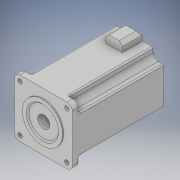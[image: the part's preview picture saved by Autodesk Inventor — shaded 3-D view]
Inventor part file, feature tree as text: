
AUTODESK INVENTOR PART (.ipt)
format: ipt  version: 2018 (Build 220112000, 112)  size: 386,048 bytes
history: native  units: mm
features: extrude x13, sketch x13, chamfer x5, projected_geometry x4, fillet x3, hole x1, plane x1
ambient origin geometry x8: Origin, YZ Plane, XZ Plane, XY Plane, X Axis, Y Axis, Z Axis, Center Point
bodies: Solid1 (feature_tree)
feature tree (40):
  extrude  "Extrusion1"  Depth=86.0mm
  extrude  "Extrusion2"  Depth=140.0mm
  extrude  "Extrusion3"  Depth=1.5mm
  hole  "Hole1"  [1 undecoded]
  plane  "Work Plane1"
  extrude  "Extrusion4"  Depth=13.0mm TaperAngle=0.0deg
  sketch  "Sketch6"  dims[d13=3.0mm d14=6.0mm d15=4.0mm d16=2.0mm d17=90.0deg d18=13.0mm d19=0.0mm d24=2.438mm d25=0.0mm]
  extrude  "Extrusion6"  Depth=69.6mm
  extrude  "Extrusion7"  Depth=120.0mm TaperAngle=0.0deg
  chamfer  "Chamfer1"  Distance=13.0mm
  fillet  "Fillet1"  Radius=8.0mm
  chamfer  "Chamfer2"  Distance=5.0mm Angle=45.0deg
  chamfer  "Chamfer3"  Distance=1.0mm Angle=45.0deg
  extrude  "Extrusion8"  Depth=56.0mm
  extrude  "Extrusion9"  Depth=3.0mm TaperAngle=45.0deg
  chamfer  "Chamfer4"  Distance=2.0mm
  fillet  "Fillet3"  Radius=15.0mm
  extrude  "Extrusion10"  Depth=15.0mm
  fillet  "Fillet4"  Radius=40.0mm
  extrude  "Extrusion11"  Depth=130.0mm TaperAngle=0.0deg
  chamfer  "Chamfer5"  Distance=2.0mm
  extrude  "Extrusion13"  Depth=8.0mm
  extrude  "Extrusion14"  Depth=2.0mm TaperAngle=0.0deg
  extrude  "Extrusion15"  Depth=2.0mm TaperAngle=45.0deg
  sketch  "Sketch1"  dims[d0=86.0mm d1=86.0mm]
  sketch  "Sketch2"  dims[d2=140.0mm d3=0.0mm d5=60.0mm]
  sketch  "Sketch3"  dims[d6=1.5mm d7=0.0mm d8=14.0mm]
  sketch  "Sketch5"  dims[d9=40.0mm d10=0.0mm d11=10.0mm d12=10.0mm]
  projected_geometry  "Projected Loop1"
  sketch  "Sketch7"  dims[d36=6.5mm d37=69.6mm]
  projected_geometry  "Projected Loop2"
  sketch  "Sketch8"  dims[d38=69.6mm d39=120.0mm d40=0.0mm]
  sketch  "Sketch9"  dims[d41=25.0mm]
  projected_geometry  "Projected Loop3"
  sketch  "Sketch10"  dims[d42=30.0mm]
  sketch  "Sketch11"  dims[d43=5.0mm d46=13.0mm d47=0.0mm]
  sketch  "Sketch13"  dims[d48=5.0mm d49=7.0mm d50=45.0deg d51=8.0mm d53=5.0mm d54=7.0mm d55=45.0deg d56=1.0mm d57=7.0mm d58=45.0deg]
  projected_geometry  "Projected Loop5"
  sketch  "Sketch14"  dims[d59=3.0mm d60=0.0mm d61=56.0mm]
  sketch  "Sketch15"  dims[d62=3.0mm d63=0.0mm d64=3.0mm d65=7.0mm d66=45.0deg d67=2.0mm d71=15.0mm d72=15.0mm d73=40.0mm d75=360.0deg d77=130.0mm d78=0.0mm d79=2.0mm d81=8.0mm d82=2.0mm d83=0.0mm d84=2.0mm d85=7.0mm d86=45.0deg d90=13.0mm d91=10.0mm d92=0.0mm d93=10.0mm d94=0.0mm d95=10.0mm d96=0.0mm]
note: 1 required parameter value undecoded (feature->parameter linkage not recoverable at this tier; creation-order binding heuristic only, values carry confidence <= 0.55)
